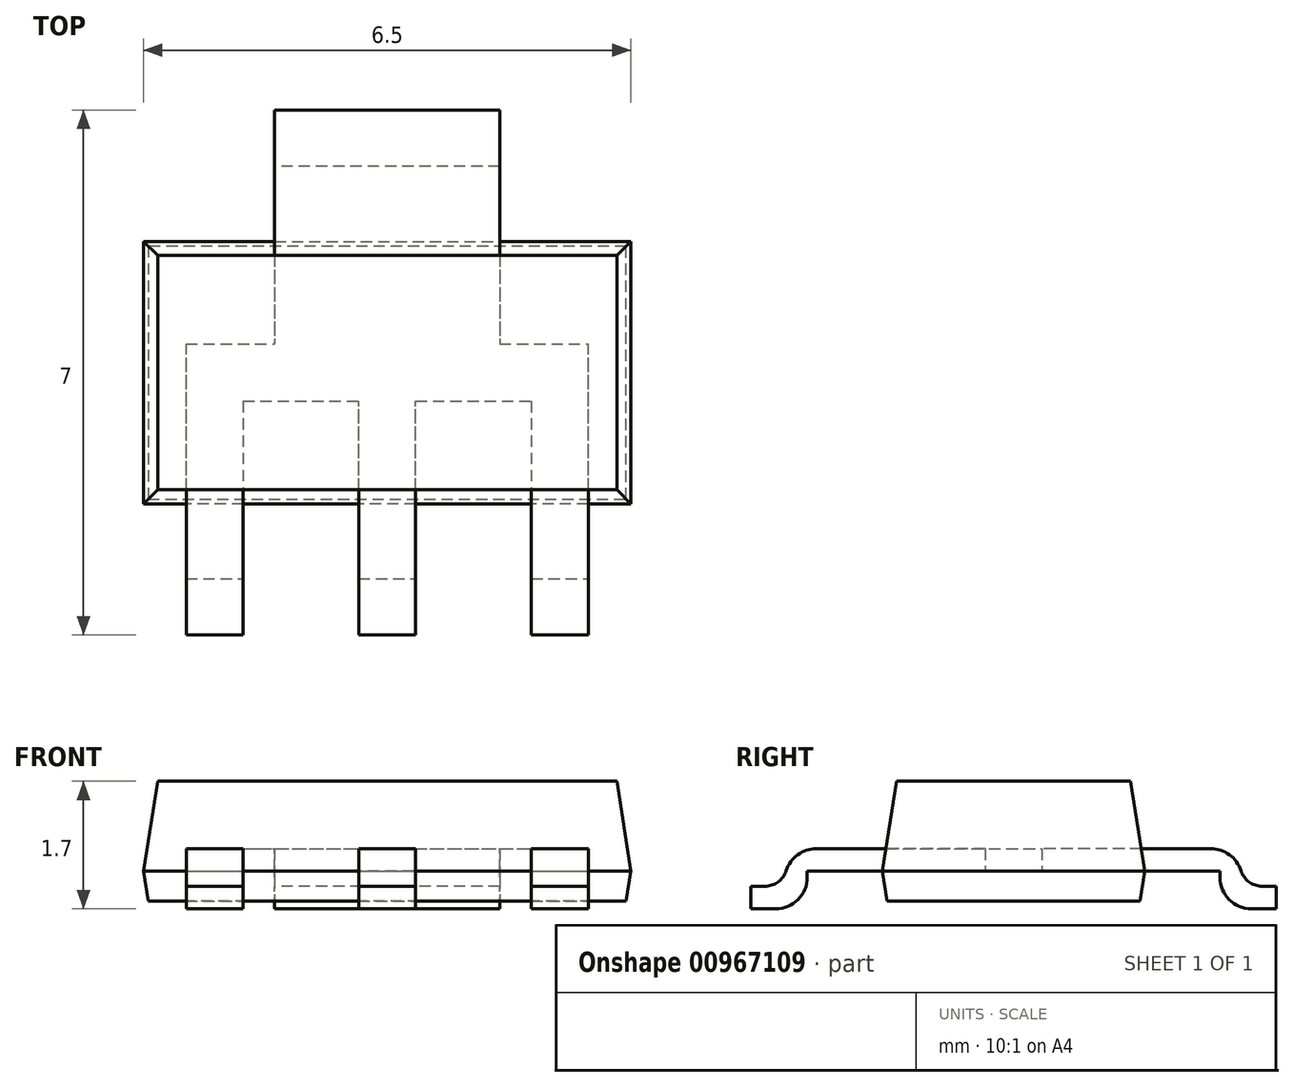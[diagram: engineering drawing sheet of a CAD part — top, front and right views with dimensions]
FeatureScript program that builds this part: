
annotation { "Feature Type Name" : "Feature", "Feature Type Description" : "" }
export const myFeature = defineFeature(function(context is Context, id is Id, definition is map)
    precondition{}
    {
        {
            assignVariable(context, id + "F0", {"name" : "A2", "anyValue" : 1.6});
        }
        {
            assignVariable(context, id + "F1", {"name" : "A1", "anyValue" : 0.1});
        }
        {
            assignVariable(context, id + "F2", {"name" : "c", "anyValue" : 0.3});
        }
        {
            var Q0;
            Q0=qCreatedBy(makeId("Top.planeOp"),FACE);
            var sketch = newSketch(context, id + "F3", { "sketchPlane" : qUnion([Q0])});
            skLineSegment(sketch, "E0.bottom", {"start": v(3.25, -1.75) * mm, "end": v(-3.25, -1.75) * mm});
            skLineSegment(sketch, "E0.top", {"start": v(3.25, 1.75) * mm, "end": v(-3.25, 1.75) * mm});
            skLineSegment(sketch, "E0.left", {"start": v(3.25, -1.75) * mm, "end": v(3.25, 1.75) * mm});
            skLineSegment(sketch, "E0.right", {"start": v(-3.25, -1.75) * mm, "end": v(-3.25, 1.75) * mm});
            skPoint(sketch, "E0.middle", {"position": v(0, 0) * mm});
            skLineSegment(sketch, "E1.bottom", {"start": v(-1.92, 0) * mm, "end": v(-2.68, 0) * mm});
            skLineSegment(sketch, "E1.top", {"start": v(-1.92, -3.5) * mm, "end": v(-2.68, -3.5) * mm});
            skLineSegment(sketch, "E1.left", {"start": v(-1.92, 0) * mm, "end": v(-1.92, -3.5) * mm});
            skLineSegment(sketch, "E1.right", {"start": v(-2.68, 0) * mm, "end": v(-2.68, -3.5) * mm});
            skPoint(sketch, "E1.middle", {"position": v(-2.3, -1.75) * mm});
            skLineSegment(sketch, "E2.bottom", {"start": v(0.38, -3.5) * mm, "end": v(-0.38, -3.5) * mm});
            skLineSegment(sketch, "E2.top", {"start": v(0.38, 0) * mm, "end": v(-0.38, 0) * mm});
            skLineSegment(sketch, "E2.left", {"start": v(0.38, -3.5) * mm, "end": v(0.38, 0) * mm});
            skLineSegment(sketch, "E2.right", {"start": v(-0.38, -3.5) * mm, "end": v(-0.38, 0) * mm});
            skPoint(sketch, "E2.middle", {"position": v(0, -1.75) * mm});
            skLineSegment(sketch, "E3.bottom", {"start": v(1.92, 0) * mm, "end": v(2.68, 0) * mm});
            skLineSegment(sketch, "E3.top", {"start": v(1.92, -3.5) * mm, "end": v(2.68, -3.5) * mm});
            skLineSegment(sketch, "E3.left", {"start": v(1.92, 0) * mm, "end": v(1.92, -3.5) * mm});
            skLineSegment(sketch, "E3.right", {"start": v(2.68, 0) * mm, "end": v(2.68, -3.5) * mm});
            skPoint(sketch, "E3.middle", {"position": v(2.3, -1.75) * mm});
            skLineSegment(sketch, "E4.bottom", {"start": v(1.5, 3.5) * mm, "end": v(-1.5, 3.5) * mm});
            skLineSegment(sketch, "E4.top", {"start": v(1.5, 0) * mm, "end": v(-1.5, 0) * mm});
            skLineSegment(sketch, "E4.left", {"start": v(1.5, 3.5) * mm, "end": v(1.5, 0) * mm});
            skLineSegment(sketch, "E4.right", {"start": v(-1.5, 3.5) * mm, "end": v(-1.5, 0) * mm});
            skPoint(sketch, "E4.middle", {"position": v(0, 1.75) * mm});
            skLineSegment(sketch, "E5", {"start": v(-2.3, -1.75) * mm, "end": v(0, -1.75) * mm, "construction": true});
            skLineSegment(sketch, "E6", {"start": v(0, -1.75) * mm, "end": v(2.3, -1.75) * mm, "construction": true});
            skLineSegment(sketch, "E7", {"start": v(0, 0) * mm, "end": v(0, 1.75) * mm, "construction": true});
            skLineSegment(sketch, "E8", {"start": v(0, 0) * mm, "end": v(0, -1.75) * mm, "construction": true});
            skLineSegment(sketch, "E9.bottom", {"start": v(-2.68, -0.38) * mm, "end": v(2.68, -0.38) * mm});
            skLineSegment(sketch, "E9.top", {"start": v(-2.68, 0.38) * mm, "end": v(2.68, 0.38) * mm});
            skLineSegment(sketch, "E9.left", {"start": v(-2.68, -0.38) * mm, "end": v(-2.68, 0.38) * mm});
            skLineSegment(sketch, "E9.right", {"start": v(2.68, -0.38) * mm, "end": v(2.68, 0.38) * mm});
            skLineSegment(sketch, "E10", {"start": v(-2.68, -2.75) * mm, "end": v(2.68, -2.75) * mm});
            skLineSegment(sketch, "E11", {"start": v(2.68, -3.05) * mm, "end": v(-2.68, -3.05) * mm});
            skLineSegment(sketch, "E12", {"start": v(-1.5, 3.05) * mm, "end": v(1.5, 3.05) * mm});
            skLineSegment(sketch, "E13", {"start": v(1.5, 2.75) * mm, "end": v(-1.5, 2.75) * mm});
            skSolve(sketch);
        }
        {
            var Q0;
            {var subQ0=sQuery(id+"F3.wireOp",EDGE,"E0.left");Q0=makeQuery(id+"F3.imprint","IMPRINT",FACE,{"disambiguationData":[TD([[makeQuery(id+"F3.imprint","IMPRINT",EDGE,{"derivedFrom":subQ0}),1.0]])]});}
            var Q1;
            {var subQ0=sQuery(id+"F3.wireOp",EDGE,"E4.left");var subQ1=sQuery(id+"F3.wireOp",EDGE,"E0.top");var subQ2=makeQuery(id+"F3.imprint","INTERSECT",VERTEX,{"derivedFrom":[subQ1,subQ0]});Q1=makeQuery(id+"F3.imprint","IMPRINT",FACE,{"disambiguationData":[TD([[makeQuery(id+"F3.imprint","IMPRINT",EDGE,{"disambiguationData":[TD([[subQ2,-1.0]])],"derivedFrom":subQ1}),1.0]])]});}
            var Q2;
            {var subQ0=sQuery(id+"F3.wireOp",EDGE,"E3.left");var subQ1=sQuery(id+"F3.wireOp",EDGE,"E0.bottom");var subQ2=makeQuery(id+"F3.imprint","INTERSECT",VERTEX,{"derivedFrom":[subQ1,subQ0]});Q2=makeQuery(id+"F3.imprint","IMPRINT",FACE,{"disambiguationData":[TD([[makeQuery(id+"F3.imprint","IMPRINT",EDGE,{"disambiguationData":[TD([[subQ2,-1.0]])],"derivedFrom":subQ1}),-1.0]])]});}
            var Q3;
            {var subQ5=sQuery(id+"F3.wireOp",EDGE,"E2.top");Q3=makeQuery(id+"F3.imprint","IMPRINT",FACE,{"disambiguationData":[TD([[makeQuery(id+"F3.imprint","IMPRINT",EDGE,{"derivedFrom":subQ5}),-1.0]])]});}
            var Q4;
            {var subQ9=sQuery(id+"F3.wireOp",EDGE,"E3.bottom");Q4=makeQuery(id+"F3.imprint","IMPRINT",FACE,{"disambiguationData":[TD([[makeQuery(id+"F3.imprint","IMPRINT",EDGE,{"derivedFrom":subQ9}),1.0]])]});}
            var Q5;
            {var subQ0=sQuery(id+"F3.wireOp",EDGE,"E3.bottom");Q5=makeQuery(id+"F3.imprint","IMPRINT",FACE,{"disambiguationData":[TD([[makeQuery(id+"F3.imprint","IMPRINT",EDGE,{"derivedFrom":subQ0}),-1.0]])]});}
            var Q6;
            {var subQ0=sQuery(id+"F3.wireOp",EDGE,"E3.left");var subQ1=sQuery(id+"F3.wireOp",EDGE,"E0.bottom");var subQ2=makeQuery(id+"F3.imprint","INTERSECT",VERTEX,{"derivedFrom":[subQ1,subQ0]});Q6=makeQuery(id+"F3.imprint","IMPRINT",FACE,{"disambiguationData":[TD([[makeQuery(id+"F3.imprint","IMPRINT",EDGE,{"disambiguationData":[TD([[subQ2,1.0]])],"derivedFrom":subQ1}),-1.0]])]});}
            var Q7;
            {var subQ0=sQuery(id+"F3.wireOp",EDGE,"E2.left");var subQ1=sQuery(id+"F3.wireOp",EDGE,"E0.bottom");var subQ2=makeQuery(id+"F3.imprint","INTERSECT",VERTEX,{"derivedFrom":[subQ1,subQ0]});Q7=makeQuery(id+"F3.imprint","IMPRINT",FACE,{"disambiguationData":[TD([[makeQuery(id+"F3.imprint","IMPRINT",EDGE,{"disambiguationData":[TD([[subQ2,-1.0]])],"derivedFrom":subQ1}),-1.0]])]});}
            var Q8;
            {var subQ0=sQuery(id+"F3.wireOp",EDGE,"E2.top");Q8=makeQuery(id+"F3.imprint","IMPRINT",FACE,{"disambiguationData":[TD([[makeQuery(id+"F3.imprint","IMPRINT",EDGE,{"derivedFrom":subQ0}),1.0]])]});}
            var Q9;
            {var subQ0=sQuery(id+"F3.wireOp",EDGE,"E2.right");var subQ1=sQuery(id+"F3.wireOp",EDGE,"E0.bottom");var subQ2=makeQuery(id+"F3.imprint","INTERSECT",VERTEX,{"derivedFrom":[subQ1,subQ0]});Q9=makeQuery(id+"F3.imprint","IMPRINT",FACE,{"disambiguationData":[TD([[makeQuery(id+"F3.imprint","IMPRINT",EDGE,{"disambiguationData":[TD([[subQ2,-1.0]])],"derivedFrom":subQ1}),-1.0]])]});}
            var Q10;
            {var subQ7=sQuery(id+"F3.wireOp",EDGE,"E1.bottom");Q10=makeQuery(id+"F3.imprint","IMPRINT",FACE,{"disambiguationData":[TD([[makeQuery(id+"F3.imprint","IMPRINT",EDGE,{"derivedFrom":subQ7}),-1.0]])]});}
            var Q11;
            {var subQ0=sQuery(id+"F3.wireOp",EDGE,"E0.right");Q11=makeQuery(id+"F3.imprint","IMPRINT",FACE,{"disambiguationData":[TD([[makeQuery(id+"F3.imprint","IMPRINT",EDGE,{"derivedFrom":subQ0}),-1.0]])]});}
            var Q12;
            {var subQ0=sQuery(id+"F3.wireOp",EDGE,"E1.bottom");Q12=makeQuery(id+"F3.imprint","IMPRINT",FACE,{"disambiguationData":[TD([[makeQuery(id+"F3.imprint","IMPRINT",EDGE,{"derivedFrom":subQ0}),1.0]])]});}
            var Q13;
            {var subQ0=sQuery(id+"F3.wireOp",EDGE,"E1.right");var subQ1=sQuery(id+"F3.wireOp",EDGE,"E0.bottom");var subQ2=makeQuery(id+"F3.imprint","INTERSECT",VERTEX,{"derivedFrom":[subQ1,subQ0]});Q13=makeQuery(id+"F3.imprint","IMPRINT",FACE,{"disambiguationData":[TD([[makeQuery(id+"F3.imprint","IMPRINT",EDGE,{"disambiguationData":[TD([[subQ2,1.0]])],"derivedFrom":subQ1}),-1.0]])]});}
            extrude(context, id + "F4", {"entities" : qUnion([Q0, Q1, Q2, Q3, Q4, Q5, Q6, Q7, Q8, Q9, Q10, Q11, Q12, Q13]), "depth" : (getVariable(context, 'A2') - 0.4) * mm, "offsetDistance" : 25 * mm, "hasDraft" : true, "draftAngle" : 9 * degree, "draftPullDirection" : true});
        }
        {
            var Q0;
            Q0=makeQuery(id+"F4.opExtrude","CAP_FACE",FACE,{"disambiguationData":[OSD([sQuery(id+"F3.wireOp",EDGE,"E0.bottom"),sQuery(id+"F3.wireOp",EDGE,"E0.top"),sQuery(id+"F3.wireOp",EDGE,"E0.left"),sQuery(id+"F3.wireOp",EDGE,"E0.right")])],"isStart":true});
            extrude(context, id + "F5", {"entities" : qUnion([Q0]), "operationType" : NewBodyOperationType.ADD, "depth" : 0.4 * mm, "offsetDistance" : 25 * mm, "hasDraft" : true, "draftAngle" : 9 * degree, "draftPullDirection" : true});
        }
        {
            var Q0;
            {var subQ0=sQuery(id+"F3.wireOp",EDGE,"E4.left");var subQ1=sQuery(id+"F3.wireOp",EDGE,"E0.top");var subQ2=makeQuery(id+"F3.imprint","INTERSECT",VERTEX,{"derivedFrom":[subQ1,subQ0]});Q0=makeQuery(id+"F3.imprint","IMPRINT",FACE,{"disambiguationData":[TD([[makeQuery(id+"F3.imprint","IMPRINT",EDGE,{"disambiguationData":[TD([[subQ2,-1.0]])],"derivedFrom":subQ1}),1.0]])]});}
            var Q1;
            {var subQ5=sQuery(id+"F3.wireOp",EDGE,"E2.top");Q1=makeQuery(id+"F3.imprint","IMPRINT",FACE,{"disambiguationData":[TD([[makeQuery(id+"F3.imprint","IMPRINT",EDGE,{"derivedFrom":subQ5}),-1.0]])]});}
            var Q2;
            {var subQ7=sQuery(id+"F3.wireOp",EDGE,"E1.bottom");Q2=makeQuery(id+"F3.imprint","IMPRINT",FACE,{"disambiguationData":[TD([[makeQuery(id+"F3.imprint","IMPRINT",EDGE,{"derivedFrom":subQ7}),-1.0]])]});}
            var Q3;
            {var subQ0=sQuery(id+"F3.wireOp",EDGE,"E1.right");var subQ1=sQuery(id+"F3.wireOp",EDGE,"E0.bottom");var subQ2=makeQuery(id+"F3.imprint","INTERSECT",VERTEX,{"derivedFrom":[subQ1,subQ0]});Q3=makeQuery(id+"F3.imprint","IMPRINT",FACE,{"disambiguationData":[TD([[makeQuery(id+"F3.imprint","IMPRINT",EDGE,{"disambiguationData":[TD([[subQ2,1.0]])],"derivedFrom":subQ1}),-1.0]])]});}
            var Q4;
            {var subQ0=sQuery(id+"F3.wireOp",EDGE,"E1.bottom");Q4=makeQuery(id+"F3.imprint","IMPRINT",FACE,{"disambiguationData":[TD([[makeQuery(id+"F3.imprint","IMPRINT",EDGE,{"derivedFrom":subQ0}),1.0]])]});}
            var Q5;
            {var subQ0=sQuery(id+"F3.wireOp",EDGE,"E2.left");var subQ1=sQuery(id+"F3.wireOp",EDGE,"E0.bottom");var subQ2=makeQuery(id+"F3.imprint","INTERSECT",VERTEX,{"derivedFrom":[subQ1,subQ0]});Q5=makeQuery(id+"F3.imprint","IMPRINT",FACE,{"disambiguationData":[TD([[makeQuery(id+"F3.imprint","IMPRINT",EDGE,{"disambiguationData":[TD([[subQ2,-1.0]])],"derivedFrom":subQ1}),-1.0]])]});}
            var Q6;
            {var subQ9=sQuery(id+"F3.wireOp",EDGE,"E3.bottom");Q6=makeQuery(id+"F3.imprint","IMPRINT",FACE,{"disambiguationData":[TD([[makeQuery(id+"F3.imprint","IMPRINT",EDGE,{"derivedFrom":subQ9}),1.0]])]});}
            var Q7;
            {var subQ0=sQuery(id+"F3.wireOp",EDGE,"E2.top");Q7=makeQuery(id+"F3.imprint","IMPRINT",FACE,{"disambiguationData":[TD([[makeQuery(id+"F3.imprint","IMPRINT",EDGE,{"derivedFrom":subQ0}),1.0]])]});}
            var Q8;
            {var subQ0=sQuery(id+"F3.wireOp",EDGE,"E3.left");var subQ1=sQuery(id+"F3.wireOp",EDGE,"E0.bottom");var subQ2=makeQuery(id+"F3.imprint","INTERSECT",VERTEX,{"derivedFrom":[subQ1,subQ0]});Q8=makeQuery(id+"F3.imprint","IMPRINT",FACE,{"disambiguationData":[TD([[makeQuery(id+"F3.imprint","IMPRINT",EDGE,{"disambiguationData":[TD([[subQ2,1.0]])],"derivedFrom":subQ1}),-1.0]])]});}
            var Q9;
            {var subQ0=sQuery(id+"F3.wireOp",EDGE,"E3.bottom");Q9=makeQuery(id+"F3.imprint","IMPRINT",FACE,{"disambiguationData":[TD([[makeQuery(id+"F3.imprint","IMPRINT",EDGE,{"derivedFrom":subQ0}),-1.0]])]});}
            var Q10;
            {var subQ0=sQuery(id+"F3.wireOp",EDGE,"E1.right");var subQ1=sQuery(id+"F3.wireOp",EDGE,"E0.bottom");var subQ2=makeQuery(id+"F3.imprint","INTERSECT",VERTEX,{"derivedFrom":[subQ1,subQ0]});Q10=makeQuery(id+"F3.imprint","IMPRINT",FACE,{"disambiguationData":[TD([[makeQuery(id+"F3.imprint","IMPRINT",EDGE,{"disambiguationData":[TD([[subQ2,1.0]])],"derivedFrom":subQ1}),1.0]])]});}
            var Q11;
            {var subQ0=sQuery(id+"F3.wireOp",EDGE,"E11");var subQ1=sQuery(id+"F3.wireOp",EDGE,"E1.left");var subQ2=makeQuery(id+"F3.imprint","INTERSECT",VERTEX,{"derivedFrom":[subQ1,subQ0]});Q11=makeQuery(id+"F3.imprint","IMPRINT",FACE,{"disambiguationData":[TD([[makeQuery(id+"F3.imprint","IMPRINT",EDGE,{"disambiguationData":[TD([[subQ2,1.0]])],"derivedFrom":subQ1}),-1.0]])]});}
            var Q12;
            {var subQ0=sQuery(id+"F3.wireOp",EDGE,"E2.left");var subQ1=sQuery(id+"F3.wireOp",EDGE,"E0.bottom");var subQ2=makeQuery(id+"F3.imprint","INTERSECT",VERTEX,{"derivedFrom":[subQ1,subQ0]});Q12=makeQuery(id+"F3.imprint","IMPRINT",FACE,{"disambiguationData":[TD([[makeQuery(id+"F3.imprint","IMPRINT",EDGE,{"disambiguationData":[TD([[subQ2,-1.0]])],"derivedFrom":subQ1}),1.0]])]});}
            var Q13;
            {var subQ0=sQuery(id+"F3.wireOp",EDGE,"E10");var subQ1=sQuery(id+"F3.wireOp",EDGE,"E2.left");var subQ2=makeQuery(id+"F3.imprint","INTERSECT",VERTEX,{"derivedFrom":[subQ1,subQ0]});Q13=makeQuery(id+"F3.imprint","IMPRINT",FACE,{"disambiguationData":[TD([[makeQuery(id+"F3.imprint","IMPRINT",EDGE,{"disambiguationData":[TD([[subQ2,1.0]])],"derivedFrom":subQ1}),1.0]])]});}
            var Q14;
            {var subQ0=sQuery(id+"F3.wireOp",EDGE,"E3.left");var subQ1=sQuery(id+"F3.wireOp",EDGE,"E0.bottom");var subQ2=makeQuery(id+"F3.imprint","INTERSECT",VERTEX,{"derivedFrom":[subQ1,subQ0]});Q14=makeQuery(id+"F3.imprint","IMPRINT",FACE,{"disambiguationData":[TD([[makeQuery(id+"F3.imprint","IMPRINT",EDGE,{"disambiguationData":[TD([[subQ2,1.0]])],"derivedFrom":subQ1}),1.0]])]});}
            var Q15;
            {var subQ0=sQuery(id+"F3.wireOp",EDGE,"E11");var subQ1=sQuery(id+"F3.wireOp",EDGE,"E3.left");var subQ2=makeQuery(id+"F3.imprint","INTERSECT",VERTEX,{"derivedFrom":[subQ1,subQ0]});Q15=makeQuery(id+"F3.imprint","IMPRINT",FACE,{"disambiguationData":[TD([[makeQuery(id+"F3.imprint","IMPRINT",EDGE,{"disambiguationData":[TD([[subQ2,1.0]])],"derivedFrom":subQ1}),1.0]])]});}
            var Q16;
            {var subQ5=sQuery(id+"F3.wireOp",EDGE,"E13");Q16=makeQuery(id+"F3.imprint","IMPRINT",FACE,{"disambiguationData":[TD([[makeQuery(id+"F3.imprint","IMPRINT",EDGE,{"derivedFrom":subQ5}),1.0]])]});}
            var Q17;
            {var subQ2=sQuery(id+"F3.wireOp",EDGE,"E12");Q17=makeQuery(id+"F3.imprint","IMPRINT",FACE,{"disambiguationData":[TD([[makeQuery(id+"F3.imprint","IMPRINT",EDGE,{"derivedFrom":subQ2}),-1.0]])]});}
            extrude(context, id + "F6", {"entities" : qUnion([Q0, Q1, Q2, Q3, Q4, Q5, Q6, Q7, Q8, Q9, Q10, Q11, Q12, Q13, Q14, Q15, Q16, Q17]), "depth" : getVariable(context, 'c') * mm, "offsetDistance" : 25 * mm});
        }
        {
            var Q0;
            {var subQ0=sQuery(id+"F3.wireOp",EDGE,"E4.bottom");Q0=makeQuery(id+"F3.imprint","IMPRINT",FACE,{"disambiguationData":[TD([[makeQuery(id+"F3.imprint","IMPRINT",EDGE,{"derivedFrom":subQ0}),1.0]])]});}
            var Q1;
            {var subQ2=sQuery(id+"F3.wireOp",EDGE,"E12");Q1=makeQuery(id+"F3.imprint","IMPRINT",FACE,{"disambiguationData":[TD([[makeQuery(id+"F3.imprint","IMPRINT",EDGE,{"derivedFrom":subQ2}),-1.0]])]});}
            var Q2;
            {var subQ0=sQuery(id+"F3.wireOp",EDGE,"E11");var subQ1=sQuery(id+"F3.wireOp",EDGE,"E1.left");var subQ2=makeQuery(id+"F3.imprint","INTERSECT",VERTEX,{"derivedFrom":[subQ1,subQ0]});Q2=makeQuery(id+"F3.imprint","IMPRINT",FACE,{"disambiguationData":[TD([[makeQuery(id+"F3.imprint","IMPRINT",EDGE,{"disambiguationData":[TD([[subQ2,1.0]])],"derivedFrom":subQ1}),-1.0]])]});}
            var Q3;
            {var subQ0=sQuery(id+"F3.wireOp",EDGE,"E1.top");Q3=makeQuery(id+"F3.imprint","IMPRINT",FACE,{"disambiguationData":[TD([[makeQuery(id+"F3.imprint","IMPRINT",EDGE,{"derivedFrom":subQ0}),-1.0]])]});}
            var Q4;
            {var subQ0=sQuery(id+"F3.wireOp",EDGE,"E2.bottom");Q4=makeQuery(id+"F3.imprint","IMPRINT",FACE,{"disambiguationData":[TD([[makeQuery(id+"F3.imprint","IMPRINT",EDGE,{"derivedFrom":subQ0}),-1.0]])]});}
            var Q5;
            {var subQ0=sQuery(id+"F3.wireOp",EDGE,"E3.top");Q5=makeQuery(id+"F3.imprint","IMPRINT",FACE,{"disambiguationData":[TD([[makeQuery(id+"F3.imprint","IMPRINT",EDGE,{"derivedFrom":subQ0}),1.0]])]});}
            var Q6;
            {var subQ0=sQuery(id+"F3.wireOp",EDGE,"E10");var subQ1=sQuery(id+"F3.wireOp",EDGE,"E2.left");var subQ2=makeQuery(id+"F3.imprint","INTERSECT",VERTEX,{"derivedFrom":[subQ1,subQ0]});Q6=makeQuery(id+"F3.imprint","IMPRINT",FACE,{"disambiguationData":[TD([[makeQuery(id+"F3.imprint","IMPRINT",EDGE,{"disambiguationData":[TD([[subQ2,1.0]])],"derivedFrom":subQ1}),1.0]])]});}
            var Q7;
            {var subQ0=sQuery(id+"F3.wireOp",EDGE,"E11");var subQ1=sQuery(id+"F3.wireOp",EDGE,"E3.left");var subQ2=makeQuery(id+"F3.imprint","INTERSECT",VERTEX,{"derivedFrom":[subQ1,subQ0]});Q7=makeQuery(id+"F3.imprint","IMPRINT",FACE,{"disambiguationData":[TD([[makeQuery(id+"F3.imprint","IMPRINT",EDGE,{"disambiguationData":[TD([[subQ2,1.0]])],"derivedFrom":subQ1}),1.0]])]});}
            extrude(context, id + "F7", {"entities" : qUnion([Q0, Q1, Q2, Q3, Q4, Q5, Q6, Q7]), "operationType" : NewBodyOperationType.ADD, "oppositeDirection" : true, "depth" : (.4 + getVariable(context, 'A1')) * mm, "offsetDistance" : 25 * mm});
        }
        {
            var Q0;
            {var subQ0=sQuery(id+"F3.wireOp",EDGE,"E4.bottom");Q0=makeQuery(id+"F3.imprint","IMPRINT",FACE,{"disambiguationData":[TD([[makeQuery(id+"F3.imprint","IMPRINT",EDGE,{"derivedFrom":subQ0}),1.0]])]});}
            var Q1;
            {var subQ0=sQuery(id+"F3.wireOp",EDGE,"E1.top");Q1=makeQuery(id+"F3.imprint","IMPRINT",FACE,{"disambiguationData":[TD([[makeQuery(id+"F3.imprint","IMPRINT",EDGE,{"derivedFrom":subQ0}),-1.0]])]});}
            var Q2;
            {var subQ0=sQuery(id+"F3.wireOp",EDGE,"E2.bottom");Q2=makeQuery(id+"F3.imprint","IMPRINT",FACE,{"disambiguationData":[TD([[makeQuery(id+"F3.imprint","IMPRINT",EDGE,{"derivedFrom":subQ0}),-1.0]])]});}
            var Q3;
            {var subQ0=sQuery(id+"F3.wireOp",EDGE,"E3.top");Q3=makeQuery(id+"F3.imprint","IMPRINT",FACE,{"disambiguationData":[TD([[makeQuery(id+"F3.imprint","IMPRINT",EDGE,{"derivedFrom":subQ0}),1.0]])]});}
            extrude(context, id + "F8", {"entities" : qUnion([Q0, Q1, Q2, Q3]), "operationType" : NewBodyOperationType.REMOVE, "oppositeDirection" : true, "depth" : ((0.4 + getVariable(context, 'A1')) - getVariable(context, 'c')) * mm, "offsetDistance" : 25 * mm});
        }
        {
            var Q0;
            {var subQ0=sQuery(id+"F3.wireOp",EDGE,"E11");Q0=makeQuery(id+"F6.opExtrude","CAP_EDGE",EDGE,{"disambiguationData":[OSD([subQ0]),TDD([makeQuery(id+"F3.imprint","IMPRINT",EDGE,{"disambiguationData":[TD([[makeQuery(id+"F3.imprint","INTERSECT",VERTEX,{"derivedFrom":[sQuery(id+"F3.wireOp",EDGE,"E1.left"),subQ0]}),-1.0]])],"derivedFrom":subQ0})])],"isStart":false});}
            var Q1;
            {var subQ0=sQuery(id+"F3.wireOp",EDGE,"E11");Q1=makeQuery(id+"F6.opExtrude","CAP_EDGE",EDGE,{"disambiguationData":[OSD([subQ0]),TDD([makeQuery(id+"F3.imprint","IMPRINT",EDGE,{"disambiguationData":[TD([[makeQuery(id+"F3.imprint","INTERSECT",VERTEX,{"derivedFrom":[sQuery(id+"F3.wireOp",EDGE,"E2.right"),subQ0]}),1.0]])],"derivedFrom":subQ0})])],"isStart":false});}
            var Q2;
            {var subQ0=sQuery(id+"F3.wireOp",EDGE,"E11");Q2=makeQuery(id+"F6.opExtrude","CAP_EDGE",EDGE,{"disambiguationData":[OSD([subQ0]),TDD([makeQuery(id+"F3.imprint","IMPRINT",EDGE,{"disambiguationData":[TD([[makeQuery(id+"F3.imprint","INTERSECT",VERTEX,{"derivedFrom":[sQuery(id+"F3.wireOp",EDGE,"E3.left"),subQ0]}),1.0]])],"derivedFrom":subQ0})])],"isStart":false});}
            var Q3;
            Q3=makeQuery(id+"F6.opExtrude","CAP_EDGE",EDGE,{"disambiguationData":[OSD([sQuery(id+"F3.wireOp",EDGE,"E12")])],"isStart":false});
            var Q4;
            Q4=makeQuery(id+"F7.opExtrude","CAP_EDGE",EDGE,{"disambiguationData":[OSD([sQuery(id+"F3.wireOp",EDGE,"E13")])],"isStart":false});
            var Q5;
            {var subQ0=sQuery(id+"F3.wireOp",EDGE,"E10");Q5=makeQuery(id+"F7.opExtrude","CAP_EDGE",EDGE,{"disambiguationData":[OSD([subQ0]),TDD([makeQuery(id+"F3.imprint","IMPRINT",EDGE,{"disambiguationData":[TD([[makeQuery(id+"F3.imprint","INTERSECT",VERTEX,{"derivedFrom":[sQuery(id+"F3.wireOp",EDGE,"E3.right"),subQ0]}),1.0]])],"derivedFrom":subQ0})])],"isStart":false});}
            var Q6;
            {var subQ0=sQuery(id+"F3.wireOp",EDGE,"E10");Q6=makeQuery(id+"F7.opExtrude","CAP_EDGE",EDGE,{"disambiguationData":[OSD([subQ0]),TDD([makeQuery(id+"F3.imprint","IMPRINT",EDGE,{"disambiguationData":[TD([[makeQuery(id+"F3.imprint","INTERSECT",VERTEX,{"derivedFrom":[sQuery(id+"F3.wireOp",EDGE,"E2.left"),subQ0]}),1.0]])],"derivedFrom":subQ0})])],"isStart":false});}
            var Q7;
            {var subQ0=sQuery(id+"F3.wireOp",EDGE,"E10");Q7=makeQuery(id+"F7.opExtrude","CAP_EDGE",EDGE,{"disambiguationData":[OSD([subQ0]),TDD([makeQuery(id+"F3.imprint","IMPRINT",EDGE,{"disambiguationData":[TD([[makeQuery(id+"F3.imprint","INTERSECT",VERTEX,{"derivedFrom":[sQuery(id+"F3.wireOp",EDGE,"E1.left"),subQ0]}),1.0]])],"derivedFrom":subQ0})])],"isStart":false});}
            fillet(context, id + "F9", {"entities" : qUnion([Q0, Q1, Q2, Q3, Q4, Q5, Q6, Q7]), "radius" : getVariable(context, 'c') * 1.4 * mm, "tangentPropagation" : true, "allowEdgeOverflow" : false});
        }
        {
            var Q0;
            {var subQ0=sQuery(id+"F3.wireOp",EDGE,"E11");Q0=makeQuery(id+"F8.boolean.opBoolean","COPY",EDGE,{"derivedFrom":makeQuery(id+"F8.opExtrude","CAP_EDGE",EDGE,{"disambiguationData":[OSD([subQ0]),TDD([makeQuery(id+"F3.imprint","IMPRINT",EDGE,{"disambiguationData":[TD([[makeQuery(id+"F3.imprint","INTERSECT",VERTEX,{"derivedFrom":[sQuery(id+"F3.wireOp",EDGE,"E1.left"),subQ0]}),-1.0]])],"derivedFrom":subQ0})])],"isStart":false})});}
            var Q1;
            {var subQ0=sQuery(id+"F3.wireOp",EDGE,"E11");Q1=makeQuery(id+"F8.boolean.opBoolean","COPY",EDGE,{"derivedFrom":makeQuery(id+"F8.opExtrude","CAP_EDGE",EDGE,{"disambiguationData":[OSD([subQ0]),TDD([makeQuery(id+"F3.imprint","IMPRINT",EDGE,{"disambiguationData":[TD([[makeQuery(id+"F3.imprint","INTERSECT",VERTEX,{"derivedFrom":[sQuery(id+"F3.wireOp",EDGE,"E2.right"),subQ0]}),1.0]])],"derivedFrom":subQ0})])],"isStart":false})});}
            var Q2;
            {var subQ0=sQuery(id+"F3.wireOp",EDGE,"E11");Q2=makeQuery(id+"F8.boolean.opBoolean","COPY",EDGE,{"derivedFrom":makeQuery(id+"F8.opExtrude","CAP_EDGE",EDGE,{"disambiguationData":[OSD([subQ0]),TDD([makeQuery(id+"F3.imprint","IMPRINT",EDGE,{"disambiguationData":[TD([[makeQuery(id+"F3.imprint","INTERSECT",VERTEX,{"derivedFrom":[sQuery(id+"F3.wireOp",EDGE,"E3.left"),subQ0]}),1.0]])],"derivedFrom":subQ0})])],"isStart":false})});}
            var Q3;
            Q3=makeQuery(id+"F8.boolean.opBoolean","COPY",EDGE,{"derivedFrom":makeQuery(id+"F8.opExtrude","CAP_EDGE",EDGE,{"disambiguationData":[OSD([sQuery(id+"F3.wireOp",EDGE,"E12")])],"isStart":false})});
            var Q4;
            Q4=makeQuery(id+"F7.opExtrude","CAP_EDGE",EDGE,{"disambiguationData":[OSD([sQuery(id+"F3.wireOp",EDGE,"E13")])],"isStart":true});
            var Q5;
            {var subQ0=sQuery(id+"F3.wireOp",EDGE,"E10");Q5=makeQuery(id+"F7.opExtrude","CAP_EDGE",EDGE,{"disambiguationData":[OSD([subQ0]),TDD([makeQuery(id+"F3.imprint","IMPRINT",EDGE,{"disambiguationData":[TD([[makeQuery(id+"F3.imprint","INTERSECT",VERTEX,{"derivedFrom":[sQuery(id+"F3.wireOp",EDGE,"E3.right"),subQ0]}),1.0]])],"derivedFrom":subQ0})])],"isStart":true});}
            var Q6;
            {var subQ0=sQuery(id+"F3.wireOp",EDGE,"E10");Q6=makeQuery(id+"F7.opExtrude","CAP_EDGE",EDGE,{"disambiguationData":[OSD([subQ0]),TDD([makeQuery(id+"F3.imprint","IMPRINT",EDGE,{"disambiguationData":[TD([[makeQuery(id+"F3.imprint","INTERSECT",VERTEX,{"derivedFrom":[sQuery(id+"F3.wireOp",EDGE,"E2.left"),subQ0]}),1.0]])],"derivedFrom":subQ0})])],"isStart":true});}
            var Q7;
            {var subQ0=sQuery(id+"F3.wireOp",EDGE,"E10");Q7=makeQuery(id+"F7.opExtrude","CAP_EDGE",EDGE,{"disambiguationData":[OSD([subQ0]),TDD([makeQuery(id+"F3.imprint","IMPRINT",EDGE,{"disambiguationData":[TD([[makeQuery(id+"F3.imprint","INTERSECT",VERTEX,{"derivedFrom":[sQuery(id+"F3.wireOp",EDGE,"E1.left"),subQ0]}),1.0]])],"derivedFrom":subQ0})])],"isStart":true});}
            fillet(context, id + "F10", {"entities" : qUnion([Q0, Q1, Q2, Q3, Q4, Q5, Q6, Q7]), "radius" : getVariable(context, 'c') * mm, "tangentPropagation" : true, "allowEdgeOverflow" : false});
        }
        {
            var Q0;
            Q0=makeQuery(id+"F7.opExtrude","CAP_FACE",FACE,{"disambiguationData":[OSD([sQuery(id+"F3.wireOp",EDGE,"E1.top"),sQuery(id+"F3.wireOp",EDGE,"E1.left"),sQuery(id+"F3.wireOp",EDGE,"E1.right"),sQuery(id+"F3.wireOp",EDGE,"E10")])],"isStart":false});
            var sketch = newSketch(context, id + "F11", { "sketchPlane" : qUnion([Q0])});
            skLineSegment(sketch, "E14.bottom", {"start": v(-1.83, 2.1) * mm, "end": v(-2.78, 2.1) * mm});
            skLineSegment(sketch, "E14.top", {"start": v(-1.83, 4) * mm, "end": v(-2.78, 4) * mm});
            skLineSegment(sketch, "E14.left", {"start": v(-1.82, 2.1) * mm, "end": v(-1.82, 4) * mm});
            skLineSegment(sketch, "E14.right", {"start": v(-2.77, 2.1) * mm, "end": v(-2.77, 4) * mm});
            skPoint(sketch, "E14.middle", {"position": v(-2.3, 3.05) * mm});
            skLineSegment(sketch, "E15.bottom", {"start": v(0.48, 4) * mm, "end": v(-0.47, 4) * mm});
            skLineSegment(sketch, "E15.top", {"start": v(0.48, 2.1) * mm, "end": v(-0.47, 2.1) * mm});
            skLineSegment(sketch, "E15.left", {"start": v(0.48, 4) * mm, "end": v(0.48, 2.1) * mm});
            skLineSegment(sketch, "E15.right", {"start": v(-0.47, 4) * mm, "end": v(-0.47, 2.1) * mm});
            skPoint(sketch, "E15.middle", {"position": v(0, 3.05) * mm});
            skLineSegment(sketch, "E16.bottom", {"start": v(2.78, 2.1) * mm, "end": v(1.83, 2.1) * mm});
            skLineSegment(sketch, "E16.top", {"start": v(2.78, 4) * mm, "end": v(1.83, 4) * mm});
            skLineSegment(sketch, "E16.left", {"start": v(2.77, 2.1) * mm, "end": v(2.77, 4) * mm});
            skLineSegment(sketch, "E16.right", {"start": v(1.82, 2.1) * mm, "end": v(1.82, 4) * mm});
            skPoint(sketch, "E16.middle", {"position": v(2.3, 3.05) * mm});
            skLineSegment(sketch, "E17.bottom", {"start": v(3.25, -1.75) * mm, "end": v(-3.25, -1.75) * mm, "construction": true});
            skLineSegment(sketch, "E17.top", {"start": v(3.25, 1.75) * mm, "end": v(-3.25, 1.75) * mm, "construction": true});
            skLineSegment(sketch, "E17.left", {"start": v(3.25, -1.75) * mm, "end": v(3.25, 1.75) * mm, "construction": true});
            skLineSegment(sketch, "E17.right", {"start": v(-3.25, -1.75) * mm, "end": v(-3.25, 1.75) * mm, "construction": true});
            skPoint(sketch, "E17.middle", {"position": v(0, 0) * mm});
            skLineSegment(sketch, "E18.bottom", {"start": v(1.63, -4) * mm, "end": v(-1.62, -4) * mm});
            skLineSegment(sketch, "E18.top", {"start": v(1.63, -2.1) * mm, "end": v(-1.62, -2.1) * mm});
            skLineSegment(sketch, "E18.left", {"start": v(1.63, -4) * mm, "end": v(1.63, -2.1) * mm});
            skLineSegment(sketch, "E18.right", {"start": v(-1.62, -4) * mm, "end": v(-1.62, -2.1) * mm});
            skPoint(sketch, "E18.middle", {"position": v(0, -3.05) * mm});
            skLineSegment(sketch, "E19.bottom", {"start": v(2.78, -4) * mm, "end": v(-2.78, -4) * mm});
            skLineSegment(sketch, "E19.top", {"start": v(2.78, 4) * mm, "end": v(-2.78, 4) * mm, "construction": true});
            skLineSegment(sketch, "E19.left", {"start": v(2.77, -4) * mm, "end": v(2.77, 4) * mm, "construction": true});
            skLineSegment(sketch, "E19.right", {"start": v(-2.77, -4) * mm, "end": v(-2.77, 4) * mm, "construction": true});
            skSolve(sketch);
        }
    });
